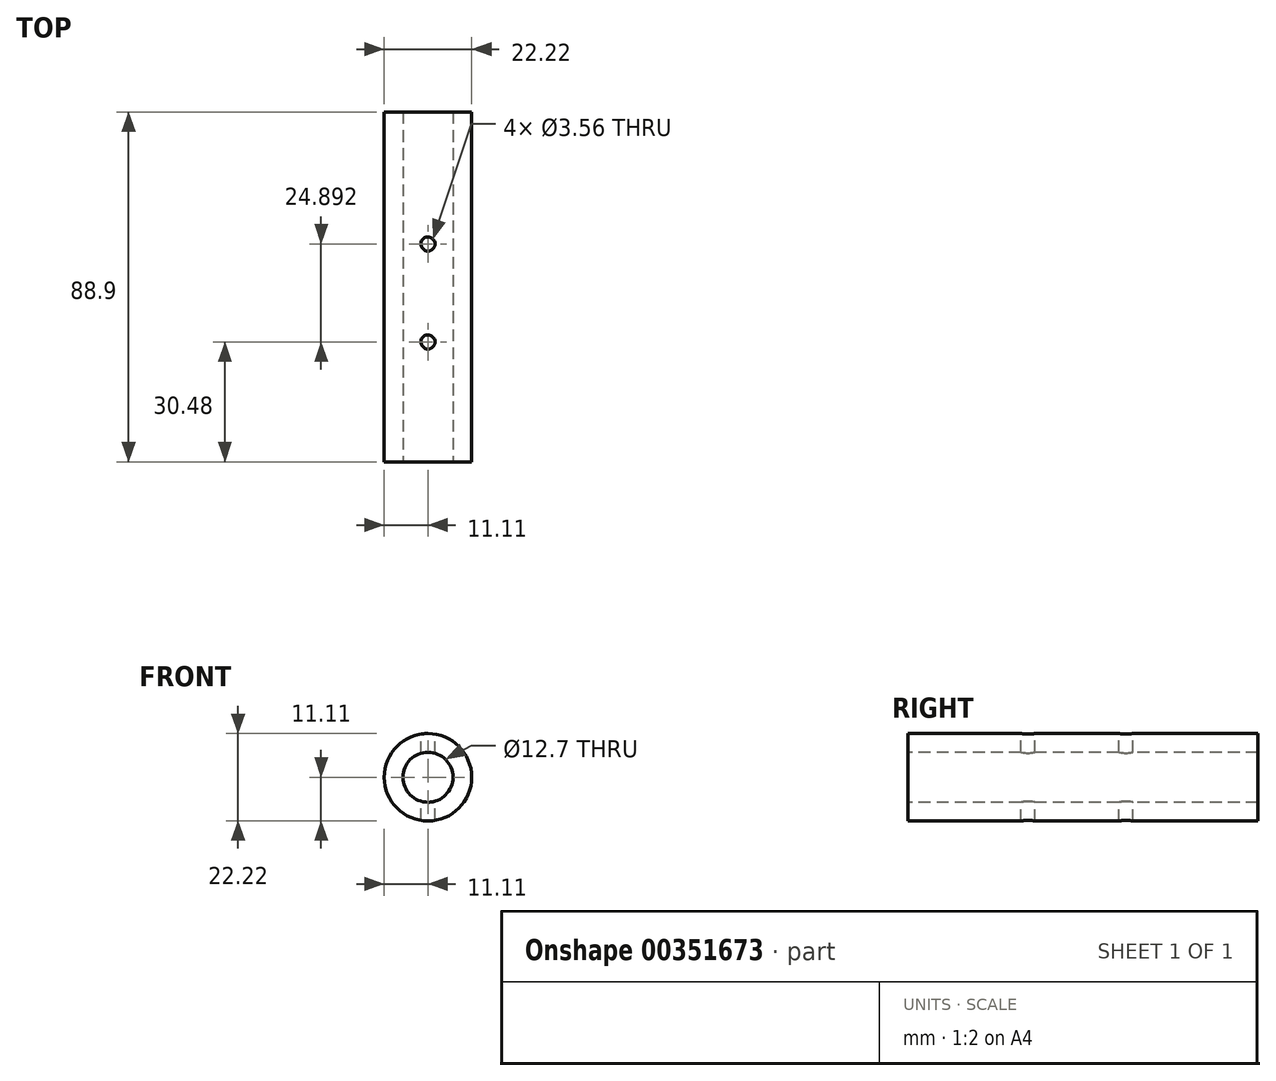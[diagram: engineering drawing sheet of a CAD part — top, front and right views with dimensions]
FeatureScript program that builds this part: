
annotation { "Feature Type Name" : "Feature", "Feature Type Description" : "" }
export const myFeature = defineFeature(function(context is Context, id is Id, definition is map)
    precondition{}
    {
        {
            var Q0;
            Q0=qCreatedBy(makeId("Front.planeOp"),FACE);
            var sketch = newSketch(context, id + "F0", { "sketchPlane" : qUnion([Q0])});
            skCircle(sketch, "E0", {"center": v(0, 0) * mm, "radius": 11.11 * mm});
            skSolve(sketch);
        }
        {
            var Q0;
            Q0 = qSketchRegion(id + "F0", true);
            extrude(context, id + "F1", {"entities" : qUnion([Q0]), "endBound" : BoundingType.SYMMETRIC, "depth" : 88.9 * mm});
        }
        {
            var Q0;
            Q0=makeQuery(id+"F1.opExtrude","CAP_FACE",FACE,{"disambiguationData":[OSD([sQuery(id+"F0.wireOp",EDGE,"E0")])],"isStart":false});
            var sketch = newSketch(context, id + "F2", { "sketchPlane" : qUnion([Q0])});
            skCircle(sketch, "E1", {"center": v(0, 0) * mm, "radius": 6.35 * mm});
            skSolve(sketch);
        }
        {
            var Q0;
            Q0 = qSketchRegion(id + "F2", true);
            extrude(context, id + "F3", {"entities" : qUnion([Q0]), "operationType" : NewBodyOperationType.REMOVE, "oppositeDirection" : true, "depth" : 88.9 * mm});
        }
        {
            var Q0;
            Q0=qCreatedBy(makeId("Top.planeOp"),FACE);
            var sketch = newSketch(context, id + "F4", { "sketchPlane" : qUnion([Q0])});
            skCircle(sketch, "E2", {"center": v(0, -13.97) * mm, "radius": 1.78 * mm});
            skSolve(sketch);
        }
        {
            var Q0;
            Q0=qCreatedBy(makeId("Top.planeOp"),FACE);
            var sketch = newSketch(context, id + "F5", { "sketchPlane" : qUnion([Q0])});
            skCircle(sketch, "E3", {"center": v(0, 10.92) * mm, "radius": 1.78 * mm});
            skSolve(sketch);
        }
        {
            var Q0;
            Q0 = qSketchRegion(id + "F5", true);
            extrude(context, id + "F6", {"entities" : qUnion([Q0]), "operationType" : NewBodyOperationType.REMOVE, "endBound" : BoundingType.SYMMETRIC, "oppositeDirection" : true, "depth" : 88.9 * mm});
        }
        {
            var Q0;
            Q0 = qSketchRegion(id + "F4", true);
            extrude(context, id + "F7", {"entities" : qUnion([Q0]), "operationType" : NewBodyOperationType.REMOVE, "endBound" : BoundingType.SYMMETRIC, "oppositeDirection" : true, "depth" : 88.9 * mm});
        }
    });
